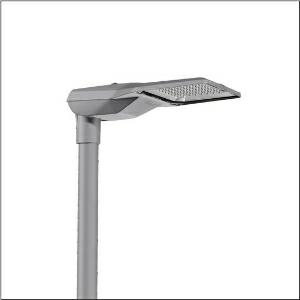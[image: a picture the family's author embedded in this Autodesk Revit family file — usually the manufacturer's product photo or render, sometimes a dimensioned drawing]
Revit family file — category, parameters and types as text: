
# Revit family: streetlight_sl_21_midi___st1_0a_5xe3d43s08lb_ab8b
name_source: partatom
category: Lighting Fixtures
units: mm (PartAtom-declared; Revit-internal decimal feet)

## family parameters
Cut with Voids When Loaded = No
Host = Face
Light Source = No
Part Type = Normal
Room Calculation Point = No
Round Connector Dimension = Use Diameter
Shared = No

## types (1)
- --- (1 x LED, 14950 lm, 99.6 W, 4000K)
    Apparent Load = 100 VA
    CIE Flux Codes = 37 72 97 100 100
    Color Rendering = 70
    Color Temperature = 4000K
    Default Elevation = 1800 mm
    Description = Streetlight SL 21 midi, mast luminaire, primary light control with lens, of PMMA, primary optical cover: cover, of toughened safety glass, transparent, light distribution: ST1.0a, light emission: direct distribution, primary light characteristic: asymmetric, installation type: side-entry, post-top, LED, High Power LED, rated luminous flux: 14.950lm, luminous efficacy: 150lm/W, light colour: 740, colour temperature: 4000K, control gear: D4i, control: overheat protection, constant luminous flux control, time-dependent luminous flux control, flexible luminous flux parameterisation, pre-setting: logarithmic dimming characteristic, mains connection: 230..240V, AC, 50/60Hz, start of lifetime: 100W, end of service life: 102W, reduction: 46W, luminaire housing, of diecast aluminium, powder-coated, Siteco® metallic grey (DB 702S), corrosivity category C5 mid according to DIN EN ISO 12944, please order mast flange separately, inclination adjustable: 0°, 5°, 10°, 15°, sealing non-destructively replaceable, multi-level sealing system, length: 644mm, width: 335mm, height: 110mm, mast flange for spigot size: 42mm (side-entry): 5XC10008XM4, 60/48mm (side-entry/post-top): 5XC10108XM2, 76/60mm (side-entry/post-top): 5XC10108XM1, mounting height: 4..8m, Smart Interface above, protection rating (complete): IP66, insulation class (complete): insulation class II (safety insulation), certification: CE, ENEC, ENEC+, VDE, impact resistance: IK10, permissible operating ambient temperature for outdoor applications: -40..+50°C, standard-compliant lighting for roads and squares, packaging unit: 1 piece

Light Distribution: ST1.0a
    Height = 111 mm
    Lamp = 1 x LED
    Lamp Light Flux = 14950 lm
    Lamp Power = 99.6 W
    Lamp count = 1
    Length = 644 mm
    Luminous efficacy = 150 lm/W
    Manufacturer = Siteco
    ModVariant = No
    Model = 5XE3D43S08LB
    Number of Poles = 1
    OnlyDefault = Yes
    Power Factor = 1
    Product Name = Streetlight SL 21 midi | ST1.0a
    Product group = mast luminaire | pylon top
    ProductGroupID = 6100
    Protection Class = Protection class II
    Protection Degree = IP 66
    RLX_Detail_Level = 1
    RLX_Emergency_Light_Flux = 0 lm
    RLX_Emergency_Type = 0
    RLX_Emergency_Type_DB = No
    RlxData = <blob elided: 26749 chars, md5=29a284f1>
    Socket = socket
    Standby Power = 0 W
    System Light Flux = 14950 lm
    System Power = 100 W
    Type Comments = factory setting: luminous flux: 100 % | dim-lin: 254 | 1020 mA
    Type Image = l_1004302.jpg
    URL = http://relux.com
    VarID = @adj_012289
    Voltage = 0 V
    Weight = 0.00 kg
    Width = 336 mm

## geometry (parser evidence)
native form markers: Blend x4, Sweep x11
no freeform markers — native parametric forms only
